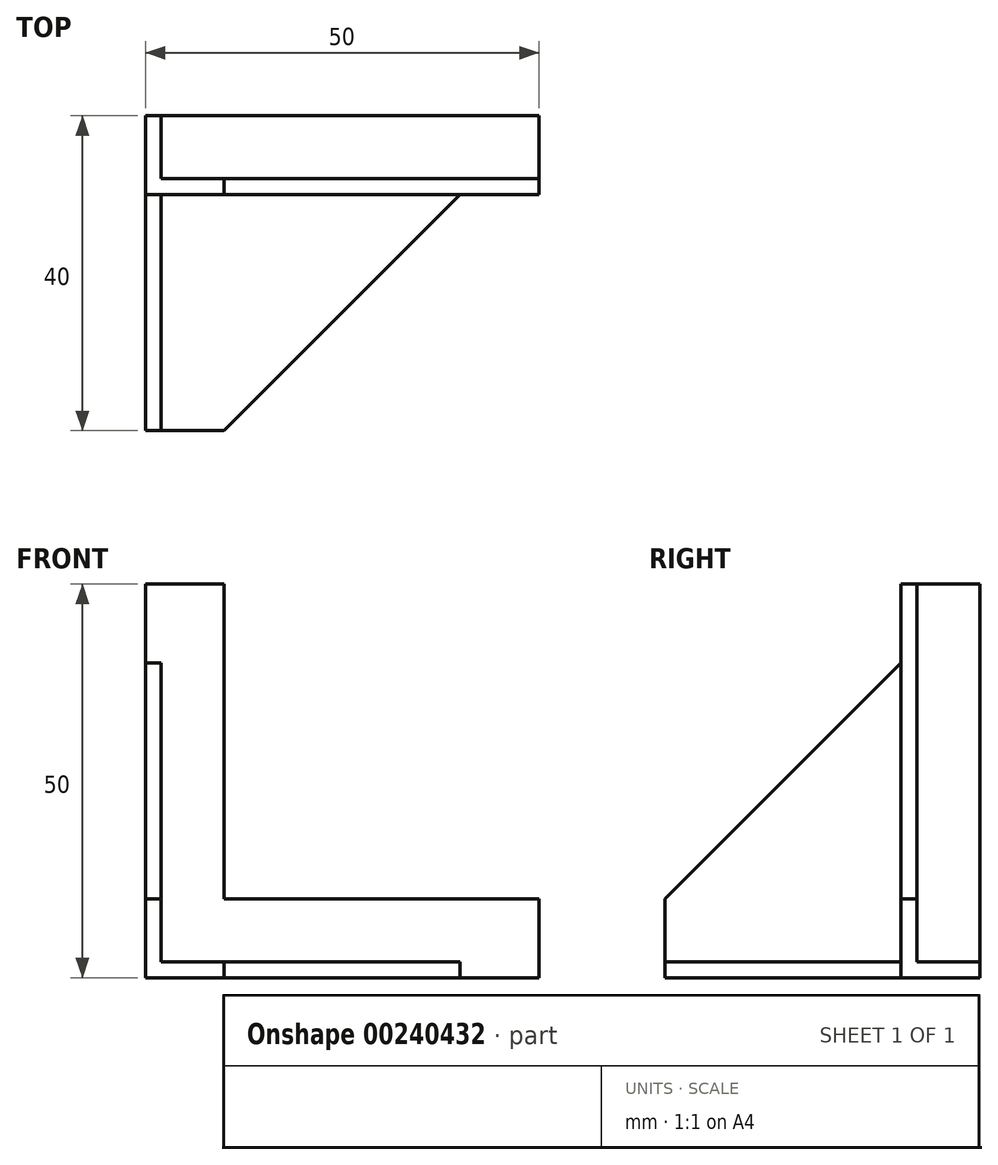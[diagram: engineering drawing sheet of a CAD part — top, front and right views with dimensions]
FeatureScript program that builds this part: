
annotation { "Feature Type Name" : "Feature", "Feature Type Description" : "" }
export const myFeature = defineFeature(function(context is Context, id is Id, definition is map)
    precondition{}
    {
        {
            var Q0;
            Q0=qCreatedBy(makeId("Top.planeOp"),FACE);
            var sketch = newSketch(context, id + "F0", { "sketchPlane" : qUnion([Q0])});
            skLineSegment(sketch, "E0", {"start": v(0, -30) * mm, "end": v(10, -30) * mm});
            skLineSegment(sketch, "E1", {"start": v(10, -30) * mm, "end": v(40, 0) * mm});
            skLineSegment(sketch, "E2", {"start": v(40, 0) * mm, "end": v(50, 0) * mm});
            skLineSegment(sketch, "E3", {"start": v(50, 0) * mm, "end": v(50, 10) * mm});
            skLineSegment(sketch, "E4", {"start": v(50, 10) * mm, "end": v(0, 10) * mm});
            skLineSegment(sketch, "E5", {"start": v(0, 10) * mm, "end": v(0, -30) * mm});
            skSolve(sketch);
        }
        {
            var Q0;
            Q0=qCreatedBy(makeId("Right.planeOp"),FACE);
            var sketch = newSketch(context, id + "F1", { "sketchPlane" : qUnion([Q0])});
            skLineSegment(sketch, "E6.0", {"start": v(10, 0) * mm, "end": v(-30, 0) * mm});
            skLineSegment(sketch, "E7", {"start": v(10, 0) * mm, "end": v(10, 50) * mm});
            skLineSegment(sketch, "E8", {"start": v(10, 50) * mm, "end": v(0, 50) * mm});
            skLineSegment(sketch, "E9", {"start": v(0, 50) * mm, "end": v(0, 40) * mm});
            skLineSegment(sketch, "E10", {"start": v(-30, 0) * mm, "end": v(-30, 10) * mm});
            skLineSegment(sketch, "E11", {"start": v(-30, 10) * mm, "end": v(0, 40) * mm});
            skSolve(sketch);
        }
        {
            var Q0;
            Q0=qCreatedBy(makeId("Front.planeOp"),FACE);
            var sketch = newSketch(context, id + "F2", { "sketchPlane" : qUnion([Q0])});
            skLineSegment(sketch, "E12.0", {"start": v(40, 0) * mm, "end": v(50, 0) * mm});
            skLineSegment(sketch, "E13.0", {"start": v(0, 50) * mm, "end": v(0, 40) * mm});
            skLineSegment(sketch, "E14", {"start": v(50, 0) * mm, "end": v(50, 10) * mm});
            skLineSegment(sketch, "E15", {"start": v(50, 10) * mm, "end": v(10, 10) * mm});
            skLineSegment(sketch, "E16", {"start": v(10, 10) * mm, "end": v(10, 50) * mm});
            skLineSegment(sketch, "E17", {"start": v(10, 50) * mm, "end": v(0, 50) * mm});
            skLineSegment(sketch, "E18", {"start": v(0, 40) * mm, "end": v(0, 0) * mm});
            skLineSegment(sketch, "E19", {"start": v(0, 0) * mm, "end": v(40, 0) * mm});
            skSolve(sketch);
        }
        {
            var Q0;
            Q0=makeQuery(id+"F1.imprint","IMPRINT",FACE,{"disambiguationData":[TD([[makeQuery(id+"F1.imprint","IMPRINT",EDGE,{"derivedFrom":sQuery(id+"F1.wireOp",EDGE,"E6.0")}),-1.0]])]});
            extrude(context, id + "F3", {"entities" : qUnion([Q0]), "depth" : 2 * mm});
        }
        {
            var Q0;
            Q0=makeQuery(id+"F0.imprint","IMPRINT",FACE,{"disambiguationData":[TD([[makeQuery(id+"F0.imprint","IMPRINT",EDGE,{"derivedFrom":sQuery(id+"F0.wireOp",EDGE,"E0")}),1.0]])]});
            extrude(context, id + "F4", {"entities" : qUnion([Q0]), "operationType" : NewBodyOperationType.ADD, "depth" : 2 * mm});
        }
        {
            var Q0;
            Q0=makeQuery(id+"F2.imprint","IMPRINT",FACE,{"disambiguationData":[TD([[makeQuery(id+"F2.imprint","IMPRINT",EDGE,{"derivedFrom":sQuery(id+"F2.wireOp",EDGE,"E12.0")}),1.0]])]});
            extrude(context, id + "F5", {"entities" : qUnion([Q0]), "operationType" : NewBodyOperationType.ADD, "oppositeDirection" : true, "depth" : 2 * mm});
        }
    });
